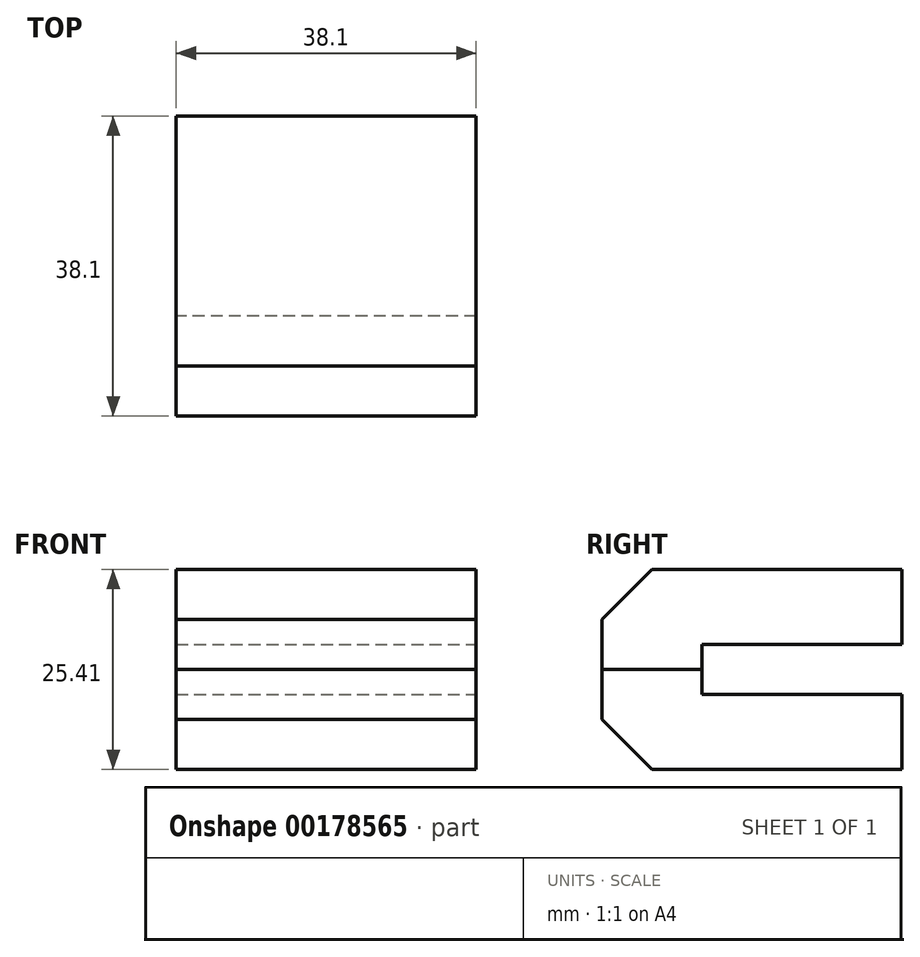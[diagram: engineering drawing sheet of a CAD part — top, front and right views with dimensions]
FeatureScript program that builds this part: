
annotation { "Feature Type Name" : "Feature", "Feature Type Description" : "" }
export const myFeature = defineFeature(function(context is Context, id is Id, definition is map)
    precondition{}
    {
        {
            var Q0;
            Q0=qCreatedBy(makeId("Top.planeOp"),FACE);
            var sketch = newSketch(context, id + "F0", { "sketchPlane" : qUnion([Q0])});
            skLineSegment(sketch, "E0.bottom", {"start": v(-19.05, -19.05) * mm, "end": v(19.05, -19.05) * mm});
            skLineSegment(sketch, "E0.top", {"start": v(-19.05, 19.05) * mm, "end": v(19.05, 19.05) * mm});
            skLineSegment(sketch, "E0.left", {"start": v(-19.05, 19.05) * mm, "end": v(-19.05, -19.05) * mm});
            skLineSegment(sketch, "E0.right", {"start": v(19.05, 19.05) * mm, "end": v(19.05, -19.05) * mm});
            skPoint(sketch, "E0.middle", {"position": v(0, 0) * mm});
            skSolve(sketch);
        }
        {
            var Q0;
            Q0=makeQuery(id+"F0.imprint","IMPRINT",FACE,{"disambiguationData":[TD([[makeQuery(id+"F0.imprint","IMPRINT",EDGE,{"derivedFrom":sQuery(id+"F0.wireOp",EDGE,"E0.bottom")}),1.0]])]});
            extrude(context, id + "F1", {"entities" : qUnion([Q0]), "depth" : 9.52 * mm});
        }
        {
            var Q0;
            Q0=makeQuery(id+"F1.opExtrude","CAP_EDGE",EDGE,{"disambiguationData":[OSD([sQuery(id+"F0.wireOp",EDGE,"E0.bottom")])],"isStart":false});
            chamfer(context, id + "F2", {"entities" : qUnion([Q0]), "width" : 6.35 * mm, "tangentPropagation" : true});
        }
        {
            var Q0;
            Q0=makeQuery(id+"F1.opExtrude","CAP_FACE",FACE,{"disambiguationData":[OSD([sQuery(id+"F0.wireOp",EDGE,"E0.bottom"),sQuery(id+"F0.wireOp",EDGE,"E0.top"),sQuery(id+"F0.wireOp",EDGE,"E0.left"),sQuery(id+"F0.wireOp",EDGE,"E0.right")])],"isStart":true});
            var sketch = newSketch(context, id + "F3", { "sketchPlane" : qUnion([Q0])});
            skLineSegment(sketch, "E1", {"start": v(19.05, 6.35) * mm, "end": v(-19.05, 6.35) * mm});
            skSolve(sketch);
        }
        {
            var Q0;
            {var subQ0=sQuery(id+"F3.wireOp",EDGE,"E1");Q0=makeQuery(id+"F3.imprint","IMPRINT",FACE,{"disambiguationData":[TD([[makeQuery(id+"F3.imprint","IMPRINT",EDGE,{"derivedFrom":subQ0}),-1.0]])]});}
            extrude(context, id + "F4", {"entities" : qUnion([Q0]), "operationType" : NewBodyOperationType.ADD, "depth" : 3.17 * mm});
        }
        {
            var Q0;
            Q0=makeQuery(id+"F1.opExtrude","SWEPT_BODY",BODY,{"disambiguationData":[OSD([sQuery(id+"F0.wireOp",EDGE,"E0.bottom"),sQuery(id+"F0.wireOp",EDGE,"E0.top"),sQuery(id+"F0.wireOp",EDGE,"E0.left"),sQuery(id+"F0.wireOp",EDGE,"E0.right")])]});
            var Q1;
            Q1=makeQuery(id+"F4.opExtrude","CAP_FACE",FACE,{"disambiguationData":[OSD([sQuery(id+"F0.wireOp",EDGE,"E0.bottom"),sQuery(id+"F0.wireOp",EDGE,"E0.left"),sQuery(id+"F0.wireOp",EDGE,"E0.right"),sQuery(id+"F3.wireOp",EDGE,"E1")])],"isStart":false});
            mirror(context, id + "F5", {"entities" : qUnion([Q0]), "mirrorPlane" : qUnion([Q1])});
        }
    });
